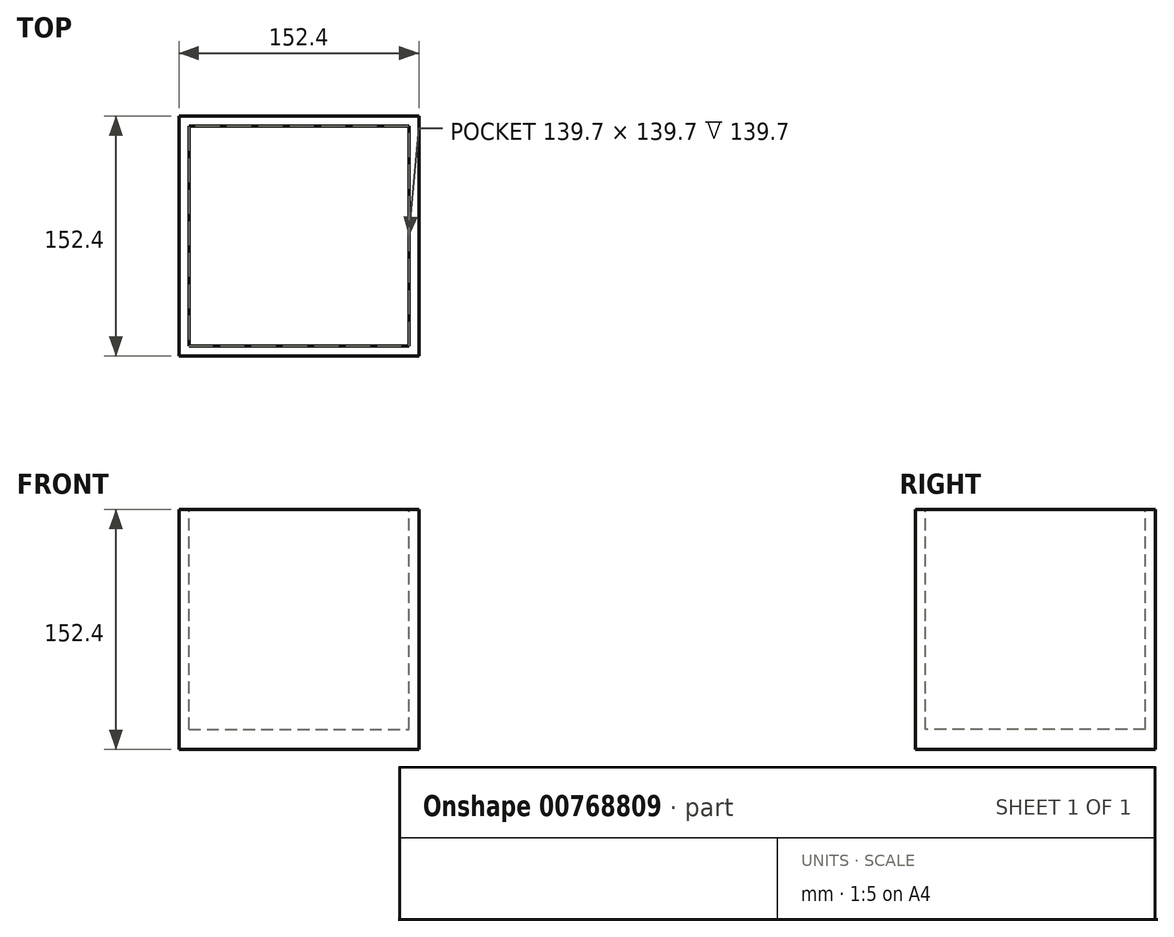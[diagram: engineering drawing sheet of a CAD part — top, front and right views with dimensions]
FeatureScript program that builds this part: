
annotation { "Feature Type Name" : "Feature", "Feature Type Description" : "" }
export const myFeature = defineFeature(function(context is Context, id is Id, definition is map)
    precondition{}
    {
        {
            var Q0;
            Q0=qCreatedBy(makeId("Top.planeOp"),FACE);
            var sketch = newSketch(context, id + "F0", { "sketchPlane" : qUnion([Q0])});
            skLineSegment(sketch, "E0.bottom", {"start": v(-76.2, 76.2) * mm, "end": v(76.2, 76.2) * mm});
            skLineSegment(sketch, "E0.top", {"start": v(-76.2, -76.2) * mm, "end": v(76.2, -76.2) * mm});
            skLineSegment(sketch, "E0.left", {"start": v(-76.2, 76.2) * mm, "end": v(-76.2, -76.2) * mm});
            skLineSegment(sketch, "E0.right", {"start": v(76.2, 76.2) * mm, "end": v(76.2, -76.2) * mm});
            skPoint(sketch, "E0.middle", {"position": v(0, 0) * mm});
            skSolve(sketch);
        }
        {
            var Q0;
            Q0=makeQuery(id+"F0.imprint","IMPRINT",FACE,{"disambiguationData":[TD([[makeQuery(id+"F0.imprint","IMPRINT",EDGE,{"derivedFrom":sQuery(id+"F0.wireOp",EDGE,"E0.bottom")}),-1.0]])]});
            var sketch = newSketch(context, id + "F1", { "sketchPlane" : qUnion([Q0])});
            skSolve(sketch);
        }
        {
            var Q0;
            Q0 = qSketchRegion(id + "F0", true);
            var Q1;
            Q1=makeQuery(id+"F1.imprint","IMPRINT",FACE,{"disambiguationData":[TD([[makeQuery(id+"F1.imprint","IMPRINT",EDGE,{"derivedFrom":makeQuery(id+"F0.imprint","IMPRINT",EDGE,{"derivedFrom":sQuery(id+"F0.wireOp",EDGE,"E0.bottom")})}),-1.0]])]});
            extrude(context, id + "F2", {"entities" : qUnion([Q0, Q1]), "depth" : 152.4 * mm, "offsetDistance" : 25.4 * mm});
        }
        {
            var Q0;
            {var subQ0=sQuery(id+"F0.wireOp",EDGE,"E0.right");var subQ1=sQuery(id+"F0.wireOp",EDGE,"E0.left");var subQ2=sQuery(id+"F0.wireOp",EDGE,"E0.top");var subQ3=sQuery(id+"F0.wireOp",EDGE,"E0.bottom");Q0=makeQuery(id+"F2.opExtrude","CAP_FACE",FACE,{"disambiguationData":[OSD([subQ3,subQ2,subQ1,subQ0]),TDD([makeQuery(id+"F1.imprint","IMPRINT",EDGE,{"derivedFrom":makeQuery(id+"F0.imprint","IMPRINT",EDGE,{"derivedFrom":subQ3})}),makeQuery(id+"F1.imprint","IMPRINT",EDGE,{"derivedFrom":makeQuery(id+"F0.imprint","IMPRINT",EDGE,{"derivedFrom":subQ2})}),makeQuery(id+"F1.imprint","IMPRINT",EDGE,{"derivedFrom":makeQuery(id+"F0.imprint","IMPRINT",EDGE,{"derivedFrom":subQ1})}),makeQuery(id+"F1.imprint","IMPRINT",EDGE,{"derivedFrom":makeQuery(id+"F0.imprint","IMPRINT",EDGE,{"derivedFrom":subQ0})})])],"isStart":false});}
            var sketch = newSketch(context, id + "F3", { "sketchPlane" : qUnion([Q0])});
            skLineSegment(sketch, "E1.bottom", {"start": v(-69.85, 69.85) * mm, "end": v(69.85, 69.85) * mm});
            skLineSegment(sketch, "E1.top", {"start": v(-69.85, -69.85) * mm, "end": v(69.85, -69.85) * mm});
            skLineSegment(sketch, "E1.left", {"start": v(-69.85, 69.85) * mm, "end": v(-69.85, -69.85) * mm});
            skLineSegment(sketch, "E1.right", {"start": v(69.85, 69.85) * mm, "end": v(69.85, -69.85) * mm});
            skPoint(sketch, "E1.middle", {"position": v(0, 0) * mm});
            skSolve(sketch);
        }
        {
            var Q0;
            Q0 = qSketchRegion(id + "F3", true);
            extrude(context, id + "F4", {"entities" : qUnion([Q0]), "operationType" : NewBodyOperationType.REMOVE, "oppositeDirection" : true, "depth" : 139.7 * mm, "offsetDistance" : 25.4 * mm});
        }
    });
